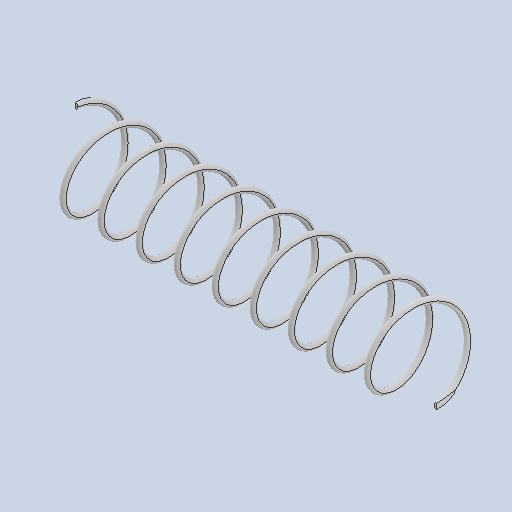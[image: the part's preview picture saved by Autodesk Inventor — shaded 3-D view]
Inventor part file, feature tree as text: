
AUTODESK INVENTOR PART (.ipt)
format: ipt  version: 2022 (Build 260153000, 153)  size: 293,376 bytes
history: native  units: in
note: dims shown in document units (in); Inventor stores cm internally (conversion verified against a paired STEP export)
features: extrude x1
ambient origin geometry x8: Origin, YZ Plane, XZ Plane, XY Plane, X Axis, Y Axis, Z Axis, Center Point
bodies: Solid1 (feature_tree)
feature tree (1):
  extrude  "Extrude1"  [1 undecoded]
note: 1 required parameter value undecoded (feature->parameter linkage not recoverable at this tier; creation-order binding heuristic only, values carry confidence <= 0.55)
